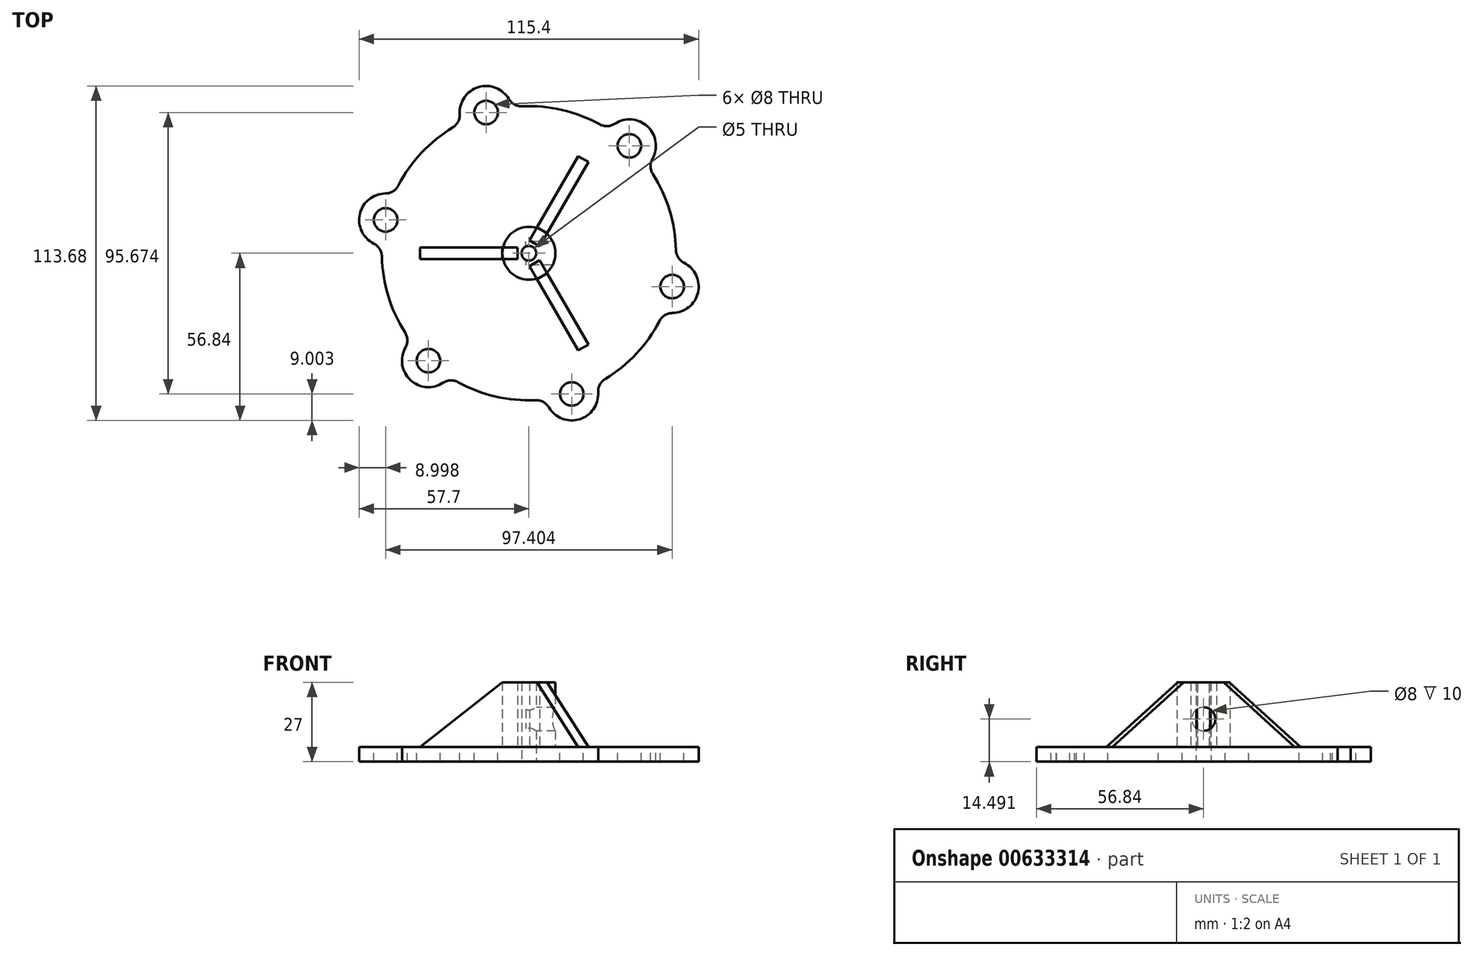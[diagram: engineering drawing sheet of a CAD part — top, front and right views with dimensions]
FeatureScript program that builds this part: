
annotation { "Feature Type Name" : "Feature", "Feature Type Description" : "" }
export const myFeature = defineFeature(function(context is Context, id is Id, definition is map)
    precondition{}
    {
        {
            var Q0;
            Q0=qCreatedBy(makeId("Top.planeOp"),FACE);
            var sketch = newSketch(context, id + "F0", { "sketchPlane" : qUnion([Q0])});
            skCircle(sketch, "E0", {"center": v(0, 0) * mm, "radius": 2.5 * mm});
            skCircle(sketch, "E1", {"center": v(0, 0) * mm, "radius": 9 * mm});
            skArc(sketch, "E2", {"start": v(49.99, 1.08) * mm, "mid": v(-48.7, 11.32) * mm, "end": v(44.39, -23.02) * mm});
            skCircle(sketch, "E3", {"center": v(48.7, -11.32) * mm, "radius": 4 * mm});
            skArc(sketch, "E4.0", {"start": v(48.78, -20.32) * mm, "mid": v(57.47, -13.36) * mm, "end": v(52.74, -3.28) * mm});
            skPoint(sketch, "E5.visualSharp", {"position": v(45.88, -19.87) * mm});
            skArc(sketch, "E5.filletArc", {"start": v(48.78, -20.32) * mm, "mid": v(46.2, -21.06) * mm, "end": v(44.39, -23.02) * mm});
            skPoint(sketch, "E6.visualSharp", {"position": v(49.94, -2.4) * mm});
            skArc(sketch, "E6.filletArc", {"start": v(49.99, 1.08) * mm, "mid": v(50.76, -1.48) * mm, "end": v(52.74, -3.28) * mm});
            skArc(sketch, "E7.1.0", {"start": v(41.99, 32.09) * mm, "mid": v(40.3, 43.1) * mm, "end": v(29.2, 44.04) * mm});
            skPoint(sketch, "E7.1.1", {"position": v(27.05, 42.05) * mm});
            skCircle(sketch, "E7.1.2", {"center": v(34.15, 36.52) * mm, "radius": 4 * mm});
            skPoint(sketch, "E7.1.3", {"position": v(40.15, 29.8) * mm});
            skArc(sketch, "E7.1.4", {"start": v(41.99, 32.09) * mm, "mid": v(41.34, 29.49) * mm, "end": v(42.13, 26.93) * mm});
            skArc(sketch, "E7.1.5", {"start": v(24.06, 43.83) * mm, "mid": v(26.66, 43.22) * mm, "end": v(29.2, 44.04) * mm});
            skArc(sketch, "E7.2.0", {"start": v(-6.8, 52.4) * mm, "mid": v(-17.17, 56.45) * mm, "end": v(-23.53, 47.32) * mm});
            skPoint(sketch, "E7.2.1", {"position": v(-22.89, 44.45) * mm});
            skCircle(sketch, "E7.2.2", {"center": v(-14.55, 47.84) * mm, "radius": 4 * mm});
            skPoint(sketch, "E7.2.3", {"position": v(-5.74, 49.67) * mm});
            skArc(sketch, "E7.2.4", {"start": v(-6.8, 52.4) * mm, "mid": v(-4.87, 50.55) * mm, "end": v(-2.26, 49.95) * mm});
            skArc(sketch, "E7.2.5", {"start": v(-25.93, 42.75) * mm, "mid": v(-24.1, 44.7) * mm, "end": v(-23.53, 47.32) * mm});
            skArc(sketch, "E7.3.0", {"start": v(-48.78, 20.32) * mm, "mid": v(-57.47, 13.36) * mm, "end": v(-52.74, 3.28) * mm});
            skPoint(sketch, "E7.3.1", {"position": v(-49.94, 2.4) * mm});
            skCircle(sketch, "E7.3.2", {"center": v(-48.7, 11.32) * mm, "radius": 4 * mm});
            skPoint(sketch, "E7.3.3", {"position": v(-45.88, 19.87) * mm});
            skArc(sketch, "E7.3.4", {"start": v(-48.78, 20.32) * mm, "mid": v(-46.2, 21.06) * mm, "end": v(-44.39, 23.02) * mm});
            skArc(sketch, "E7.3.5", {"start": v(-49.99, -1.08) * mm, "mid": v(-50.76, 1.48) * mm, "end": v(-52.74, 3.28) * mm});
            skArc(sketch, "E7.4.0", {"start": v(-41.99, -32.09) * mm, "mid": v(-40.3, -43.1) * mm, "end": v(-29.2, -44.04) * mm});
            skPoint(sketch, "E7.4.1", {"position": v(-27.05, -42.05) * mm});
            skCircle(sketch, "E7.4.2", {"center": v(-34.15, -36.52) * mm, "radius": 4 * mm});
            skPoint(sketch, "E7.4.3", {"position": v(-40.15, -29.8) * mm});
            skArc(sketch, "E7.4.4", {"start": v(-41.99, -32.09) * mm, "mid": v(-41.34, -29.49) * mm, "end": v(-42.13, -26.93) * mm});
            skArc(sketch, "E7.4.5", {"start": v(-24.06, -43.83) * mm, "mid": v(-26.66, -43.22) * mm, "end": v(-29.2, -44.04) * mm});
            skArc(sketch, "E7.5.0", {"start": v(6.8, -52.4) * mm, "mid": v(17.17, -56.45) * mm, "end": v(23.53, -47.32) * mm});
            skPoint(sketch, "E7.5.1", {"position": v(22.89, -44.45) * mm});
            skCircle(sketch, "E7.5.2", {"center": v(14.55, -47.84) * mm, "radius": 4 * mm});
            skPoint(sketch, "E7.5.3", {"position": v(5.74, -49.67) * mm});
            skArc(sketch, "E7.5.4", {"start": v(6.8, -52.4) * mm, "mid": v(4.87, -50.55) * mm, "end": v(2.26, -49.95) * mm});
            skArc(sketch, "E7.5.5", {"start": v(25.93, -42.75) * mm, "mid": v(24.1, -44.7) * mm, "end": v(23.53, -47.32) * mm});
            skSolve(sketch);
        }
        {
            var Q0;
            Q0=makeQuery(id+"F0.imprint","IMPRINT",FACE,{"disambiguationData":[TD([[makeQuery(id+"F0.imprint","IMPRINT",EDGE,{"derivedFrom":sQuery(id+"F0.wireOp",EDGE,"E0")}),-1.0]])]});
            extrude(context, id + "F1", {"entities" : qUnion([Q0]), "depth" : 22 * mm, "offsetDistance" : 25 * mm});
        }
        {
            var Q0;
            Q0=qCreatedBy(makeId("Right.planeOp"),FACE);
            var sketch = newSketch(context, id + "F2", { "sketchPlane" : qUnion([Q0])});
            skCircle(sketch, "E8", {"center": v(0, 9.5) * mm, "radius": 4 * mm});
            skSolve(sketch);
        }
        {
            var Q0;
            Q0 = qSketchRegion(id + "F2", true);
            extrude(context, id + "F3", {"entities" : qUnion([Q0]), "operationType" : NewBodyOperationType.REMOVE, "depth" : 25 * mm, "offsetDistance" : 25 * mm, "hasSecondDirection" : true, "secondDirectionOppositeDirection" : true, "secondDirectionDepth" : 1 * mm});
        }
        {
            var Q0;
            Q0=makeQuery(id+"F0.imprint","IMPRINT",FACE,{"disambiguationData":[TD([[makeQuery(id+"F0.imprint","IMPRINT",EDGE,{"derivedFrom":sQuery(id+"F0.wireOp",EDGE,"E1")}),-1.0]])]});
            var Q1;
            Q1=makeQuery(id+"F0.imprint","IMPRINT",FACE,{"disambiguationData":[TD([[makeQuery(id+"F0.imprint","IMPRINT",EDGE,{"derivedFrom":sQuery(id+"F0.wireOp",EDGE,"E7.5.0")}),1.0]])]});
            var Q2;
            Q2=makeQuery(id+"F0.imprint","IMPRINT",FACE,{"disambiguationData":[TD([[makeQuery(id+"F0.imprint","IMPRINT",EDGE,{"derivedFrom":sQuery(id+"F0.wireOp",EDGE,"E7.1.0")}),1.0]])]});
            var Q3;
            Q3=makeQuery(id+"F0.imprint","IMPRINT",FACE,{"disambiguationData":[TD([[makeQuery(id+"F0.imprint","IMPRINT",EDGE,{"derivedFrom":sQuery(id+"F0.wireOp",EDGE,"E7.2.0")}),1.0]])]});
            var Q4;
            Q4=makeQuery(id+"F0.imprint","IMPRINT",FACE,{"disambiguationData":[TD([[makeQuery(id+"F0.imprint","IMPRINT",EDGE,{"derivedFrom":sQuery(id+"F0.wireOp",EDGE,"E7.3.0")}),1.0]])]});
            var Q5;
            Q5=makeQuery(id+"F0.imprint","IMPRINT",FACE,{"disambiguationData":[TD([[makeQuery(id+"F0.imprint","IMPRINT",EDGE,{"derivedFrom":sQuery(id+"F0.wireOp",EDGE,"E7.4.0")}),1.0]])]});
            var Q6;
            Q6=makeQuery(id+"F0.imprint","IMPRINT",FACE,{"disambiguationData":[TD([[makeQuery(id+"F0.imprint","IMPRINT",EDGE,{"derivedFrom":sQuery(id+"F0.wireOp",EDGE,"E0")}),-1.0]])]});
            extrude(context, id + "F4", {"entities" : qUnion([Q0, Q1, Q2, Q3, Q4, Q5, Q6]), "operationType" : NewBodyOperationType.ADD, "oppositeDirection" : true, "depth" : 5 * mm, "offsetDistance" : 25 * mm});
        }
        {
            var Q0;
            Q0=qCreatedBy(makeId("Front.planeOp"),FACE);
            var sketch = newSketch(context, id + "F5", { "sketchPlane" : qUnion([Q0])});
            skLineSegment(sketch, "E9.0.0", {"start": v(10.55, 0) * mm, "end": v(18.33, 0) * mm});
            skLineSegment(sketch, "E9.0.1", {"start": v(18.33, 0) * mm, "end": v(25.93, 0) * mm});
            skLineSegment(sketch, "E9.0.2", {"start": v(25.93, 0) * mm, "end": v(44.39, 0) * mm});
            skLineSegment(sketch, "E9.0.3", {"start": v(44.39, 0) * mm, "end": v(48.78, 0) * mm});
            skLineSegment(sketch, "E9.0.4", {"start": v(48.78, 0) * mm, "end": v(57.7, 0) * mm});
            skLineSegment(sketch, "E9.0.5", {"start": v(52.74, 0) * mm, "end": v(49.99, 0) * mm});
            skLineSegment(sketch, "E9.0.6", {"start": v(49.99, 0) * mm, "end": v(42.13, 0) * mm});
            skLineSegment(sketch, "E9.0.7", {"start": v(42.13, 0) * mm, "end": v(36.96, 0) * mm});
            skLineSegment(sketch, "E9.0.8", {"start": v(36.96, 0) * mm, "end": v(30.15, 0) * mm});
            skLineSegment(sketch, "E9.0.9", {"start": v(31.13, 0) * mm, "end": v(24.06, 0) * mm});
            skLineSegment(sketch, "E9.0.10", {"start": v(24.06, 0) * mm, "end": v(-2.26, 0) * mm});
            skLineSegment(sketch, "E9.0.11", {"start": v(-2.26, 0) * mm, "end": v(-10.68, 0) * mm});
            skLineSegment(sketch, "E9.0.12", {"start": v(-10.55, 0) * mm, "end": v(-18.33, 0) * mm});
            skLineSegment(sketch, "E9.0.13", {"start": v(-18.33, 0) * mm, "end": v(-25.93, 0) * mm});
            skLineSegment(sketch, "E9.0.14", {"start": v(-25.93, 0) * mm, "end": v(-44.39, 0) * mm});
            skLineSegment(sketch, "E9.0.15", {"start": v(-44.39, 0) * mm, "end": v(-47.64, 0) * mm});
            skLineSegment(sketch, "E9.0.16", {"start": v(-44.7, 0) * mm, "end": v(-49.45, 0) * mm});
            skLineSegment(sketch, "E9.0.17", {"start": v(-49.45, 0) * mm, "end": v(-50, 0) * mm});
            skLineSegment(sketch, "E9.0.18", {"start": v(-49.99, 0) * mm, "end": v(-42.13, 0) * mm});
            skLineSegment(sketch, "E9.0.19", {"start": v(-42.13, 0) * mm, "end": v(-36.96, 0) * mm});
            skLineSegment(sketch, "E9.0.20", {"start": v(-36.96, 0) * mm, "end": v(-30.15, 0) * mm});
            skLineSegment(sketch, "E9.0.21", {"start": v(-31.13, 0) * mm, "end": v(-24.06, 0) * mm});
            skLineSegment(sketch, "E9.0.22", {"start": v(-24.06, 0) * mm, "end": v(2.26, 0) * mm});
            skLineSegment(sketch, "E9.0.23", {"start": v(2.26, 0) * mm, "end": v(10.68, 0) * mm});
            skLineSegment(sketch, "E10.MirrorCS", {"start": v(-36.96, 0) * mm, "end": v(-9, 22) * mm});
            skLineSegment(sketch, "E11", {"start": v(-36.96, 0) * mm, "end": v(-9, 0) * mm});
            skLineSegment(sketch, "E12.bottom", {"start": v(-9, 22) * mm, "end": v(-3.9, 22) * mm});
            skLineSegment(sketch, "E12.top", {"start": v(-9, 0) * mm, "end": v(-3.9, 0) * mm});
            skLineSegment(sketch, "E12.right", {"start": v(-3.9, 22) * mm, "end": v(-3.9, 0) * mm});
            skPoint(sketch, "E13.MirrorCS.end.orphan", {"position": v(-9, 0) * mm});
            skPoint(sketch, "E13.MirrorCS.start.orphan", {"position": v(-9, 22) * mm});
            skPoint(sketch, "E14.end.orphan", {"position": v(9, 0) * mm});
            skPoint(sketch, "E14.start.orphan", {"position": v(9, 22) * mm});
            skSolve(sketch);
        }
        {
            var Q0;
            {var subQ2=sQuery(id+"F5.wireOp",EDGE,"E10.MirrorCS");Q0=makeQuery(id+"F5.imprint","IMPRINT",FACE,{"disambiguationData":[TD([[makeQuery(id+"F5.imprint","IMPRINT",EDGE,{"derivedFrom":subQ2}),-1.0]])]});}
            extrude(context, id + "F6", {"entities" : qUnion([Q0]), "endBound" : BoundingType.SYMMETRIC, "depth" : 4 * mm, "offsetDistance" : 25 * mm});
        }
        {
            var Q0;
            Q0=makeQuery(id+"F6.opExtrude","SWEPT_BODY",BODY,{"disambiguationData":[OSD([sQuery(id+"F5.wireOp",EDGE,"E10.MirrorCS"),sQuery(id+"F5.wireOp",EDGE,"E11"),sQuery(id+"F5.wireOp",EDGE,"E12.bottom"),sQuery(id+"F5.wireOp",EDGE,"E12.top"),sQuery(id+"F5.wireOp",EDGE,"E12.right")])]});
            var Q1;
            Q1=makeQuery(id+"F1.opExtrude","CAP_EDGE",EDGE,{"disambiguationData":[OSD([sQuery(id+"F0.wireOp",EDGE,"E0")])],"isStart":false});
            circularPattern(context, id + "F7", {"entities" : qUnion([Q0]), "axis" : qUnion([Q1]), "angle" : 360 * degree, "instanceCount" : 3, "equalSpace" : true});
        }
    });
